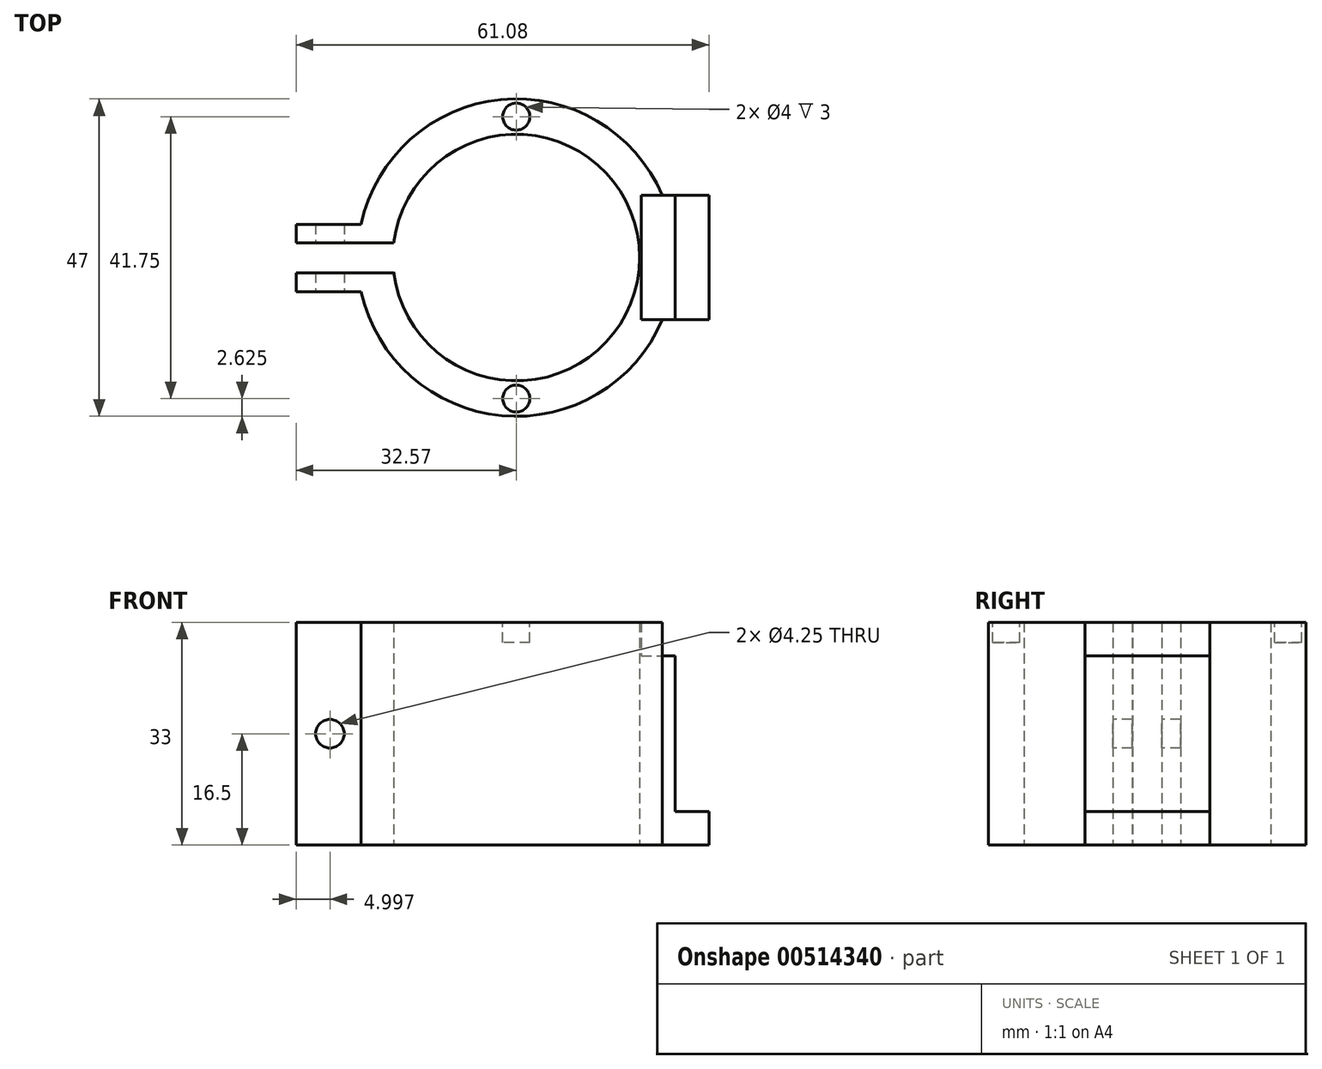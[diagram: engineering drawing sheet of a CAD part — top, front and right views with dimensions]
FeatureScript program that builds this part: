
annotation { "Feature Type Name" : "Feature", "Feature Type Description" : "" }
export const myFeature = defineFeature(function(context is Context, id is Id, definition is map)
    precondition{}
    {
        {
            var Q0;
            Q0=qCreatedBy(makeId("Top.planeOp"),FACE);
            var sketch = newSketch(context, id + "F0", { "sketchPlane" : qUnion([Q0])});
            skCircle(sketch, "E0", {"center": v(0, 0) * mm, "radius": 23.5 * mm});
            skCircle(sketch, "E1", {"center": v(0, 0) * mm, "radius": 18.25 * mm});
            skLineSegment(sketch, "E2.bottom", {"start": v(-17.57, 4.92) * mm, "end": v(-32.57, 4.92) * mm});
            skLineSegment(sketch, "E2.top", {"start": v(-17.57, -5.08) * mm, "end": v(-32.57, -5.08) * mm});
            skLineSegment(sketch, "E2.left", {"start": v(-17.57, 4.92) * mm, "end": v(-17.57, -5.08) * mm});
            skLineSegment(sketch, "E2.right", {"start": v(-32.57, 4.92) * mm, "end": v(-32.57, -5.08) * mm});
            skLineSegment(sketch, "E3.bottom", {"start": v(-18.12, 2.15) * mm, "end": v(-32.57, 2.15) * mm});
            skLineSegment(sketch, "E3.top", {"start": v(-18.12, -2.24) * mm, "end": v(-32.57, -2.24) * mm});
            skLineSegment(sketch, "E3.left", {"start": v(-18.12, 2.15) * mm, "end": v(-18.12, -2.24) * mm});
            skLineSegment(sketch, "E3.right", {"start": v(-32.57, 2.15) * mm, "end": v(-32.57, -2.24) * mm});
            skSolve(sketch);
        }
        {
            var Q0;
            {var subQ0=sQuery(id+"F0.wireOp",EDGE,"E2.bottom");var subQ1=sQuery(id+"F0.wireOp",EDGE,"E0");var subQ2=makeQuery(id+"F0.imprint","INTERSECT",VERTEX,{"derivedFrom":[subQ1,subQ0]});Q0=makeQuery(id+"F0.imprint","IMPRINT",FACE,{"disambiguationData":[TD([[makeQuery(id+"F0.imprint","IMPRINT",EDGE,{"disambiguationData":[TD([[subQ2,-1.0]])],"derivedFrom":subQ1}),-1.0]])]});}
            var Q1;
            {var subQ0=sQuery(id+"F0.wireOp",EDGE,"E2.top");var subQ1=sQuery(id+"F0.wireOp",EDGE,"E0");var subQ2=makeQuery(id+"F0.imprint","INTERSECT",VERTEX,{"derivedFrom":[subQ1,subQ0]});Q1=makeQuery(id+"F0.imprint","IMPRINT",FACE,{"disambiguationData":[TD([[makeQuery(id+"F0.imprint","IMPRINT",EDGE,{"disambiguationData":[TD([[subQ2,1.0]])],"derivedFrom":subQ1}),-1.0]])]});}
            var Q2;
            {var subQ3=sQuery(id+"F0.wireOp",EDGE,"E0");var subQ5=sQuery(id+"F0.wireOp",EDGE,"E2.bottom");var subQ9=makeQuery(id+"F0.imprint","INTERSECT",VERTEX,{"derivedFrom":[subQ3,subQ5]});Q2=makeQuery(id+"F0.imprint","IMPRINT",FACE,{"disambiguationData":[TD([[makeQuery(id+"F0.imprint","IMPRINT",EDGE,{"disambiguationData":[TD([[subQ9,1.0]])],"derivedFrom":subQ3}),1.0]])]});}
            var Q3;
            {var subQ0=sQuery(id+"F0.wireOp",EDGE,"E2.bottom");var subQ1=sQuery(id+"F0.wireOp",EDGE,"E0");var subQ2=makeQuery(id+"F0.imprint","INTERSECT",VERTEX,{"derivedFrom":[subQ1,subQ0]});Q3=makeQuery(id+"F0.imprint","IMPRINT",FACE,{"disambiguationData":[TD([[makeQuery(id+"F0.imprint","IMPRINT",EDGE,{"disambiguationData":[TD([[subQ2,-1.0]])],"derivedFrom":subQ1}),1.0]])]});}
            var Q4;
            {var subQ1=sQuery(id+"F0.wireOp",EDGE,"E2.top");var subQ5=sQuery(id+"F0.wireOp",EDGE,"E0");var subQ6=makeQuery(id+"F0.imprint","INTERSECT",VERTEX,{"derivedFrom":[subQ5,subQ1]});Q4=makeQuery(id+"F0.imprint","IMPRINT",FACE,{"disambiguationData":[TD([[makeQuery(id+"F0.imprint","IMPRINT",EDGE,{"disambiguationData":[TD([[subQ6,1.0]])],"derivedFrom":subQ5}),1.0]])]});}
            var Q5;
            Q5=qSketchRegion(id+"F2",true);
            extrude(context, id + "F1", {"entities" : qUnion([Q0, Q1, Q2, Q3, Q4, Q5]), "depth" : 33 * mm});
        }
        {
            var Q0;
            Q0=makeQuery(id+"F1.opExtrude","SWEPT_FACE",FACE,{"disambiguationData":[OSD([sQuery(id+"F0.wireOp",EDGE,"E2.top")])]});
            var sketch = newSketch(context, id + "F2", { "sketchPlane" : qUnion([Q0])});
            skCircle(sketch, "E4", {"center": v(-27.57, 16.5) * mm, "radius": 2.12 * mm});
            skSolve(sketch);
        }
        {
            var Q0;
            Q0=qCreatedBy(makeId("Top.planeOp"),FACE);
            var sketch = newSketch(context, id + "F3", { "sketchPlane" : qUnion([Q0])});
            skLineSegment(sketch, "E5.bottom", {"start": v(23.5, 9.25) * mm, "end": v(21.63, 9.25) * mm});
            skLineSegment(sketch, "E5.top", {"start": v(23.5, -9.22) * mm, "end": v(21.63, -9.22) * mm});
            skLineSegment(sketch, "E5.left", {"start": v(23.5, 9.25) * mm, "end": v(23.5, -9.22) * mm});
            skLineSegment(sketch, "E5.right", {"start": v(21.63, 9.25) * mm, "end": v(21.63, -9.22) * mm});
            skSolve(sketch);
        }
        {
            var Q0;
            Q0=makeQuery(id+"F3.imprint","IMPRINT",FACE,{"disambiguationData":[TD([[makeQuery(id+"F3.imprint","IMPRINT",EDGE,{"derivedFrom":sQuery(id+"F3.wireOp",EDGE,"E5.bottom")}),1.0]])]});
            extrude(context, id + "F4", {"entities" : qUnion([Q0]), "operationType" : NewBodyOperationType.ADD, "depth" : 33 * mm});
        }
        {
            var Q0;
            Q0=makeQuery(id+"F4.boolean.opBoolean","MERGE",FACE,{"derivedFrom":[makeQuery(id+"F1.opExtrude","CAP_FACE",FACE,{"disambiguationData":[OSD([sQuery(id+"F0.wireOp",EDGE,"E0"),sQuery(id+"F0.wireOp",EDGE,"E1"),sQuery(id+"F0.wireOp",EDGE,"E2.bottom"),sQuery(id+"F0.wireOp",EDGE,"E2.top"),sQuery(id+"F0.wireOp",EDGE,"E2.right"),sQuery(id+"F0.wireOp",EDGE,"E3.bottom"),sQuery(id+"F0.wireOp",EDGE,"E3.top"),sQuery(id+"F0.wireOp",EDGE,"E3.left")])],"isStart":false}),makeQuery(id+"FjpIeYwHbn2ZtRx_1.opExtrude","CAP_FACE",FACE,{"disambiguationData":[OSD([sQuery(id+"FtckRxJgdQJHr4S_1.wireOp",EDGE,"LJ84nlMf-35ZW-CVmp-M2o7-AWeaV5Od0gmK.bottom"),sQuery(id+"FtckRxJgdQJHr4S_1.wireOp",EDGE,"LJ84nlMf-35ZW-CVmp-M2o7-AWeaV5Od0gmK.top"),sQuery(id+"FtckRxJgdQJHr4S_1.wireOp",EDGE,"LJ84nlMf-35ZW-CVmp-M2o7-AWeaV5Od0gmK.left"),sQuery(id+"FtckRxJgdQJHr4S_1.wireOp",EDGE,"LJ84nlMf-35ZW-CVmp-M2o7-AWeaV5Od0gmK.right")])],"isStart":false}),makeQuery(id+"F4.opExtrude","CAP_FACE",FACE,{"disambiguationData":[OSD([sQuery(id+"F3.wireOp",EDGE,"E5.bottom"),sQuery(id+"F3.wireOp",EDGE,"E5.top"),sQuery(id+"F3.wireOp",EDGE,"E5.left"),sQuery(id+"F3.wireOp",EDGE,"E5.right")])],"isStart":false})]});
            var sketch = newSketch(context, id + "F5", { "sketchPlane" : qUnion([Q0])});
            skCircle(sketch, "E6", {"center": v(0, 20.88) * mm, "radius": 2 * mm});
            skCircle(sketch, "E7.1.0.0", {"center": v(0, -20.88) * mm, "radius": 2 * mm});
            skLineSegment(sketch, "E7.direction1", {"start": v(0, 20.88) * mm, "end": v(0, -20.88) * mm, "construction": true});
            skSolve(sketch);
        }
        {
            var Q0;
            Q0=qSketchRegion(id+"F5",true);
            var Q1;
            Q1=sQuery(id+"F5.wireOp",EDGE,"E6");
            var Q2;
            Q2=sQuery(id+"F5.wireOp",EDGE,"E7.1.0.0");
            extrude(context, id + "F6", {"entities" : qUnion([Q0]), "operationType" : NewBodyOperationType.REMOVE, "surfaceEntities" : qUnion([Q1, Q2]), "oppositeDirection" : true, "depth" : 3 * mm});
        }
        {
            var Q0;
            Q0=makeQuery(id+"F4.opExtrude","SWEPT_FACE",FACE,{"disambiguationData":[OSD([sQuery(id+"F3.wireOp",EDGE,"E5.left")])]});
            var sketch = newSketch(context, id + "F7", { "sketchPlane" : qUnion([Q0])});
            skLineSegment(sketch, "E8.bottom", {"start": v(-9.22, 5) * mm, "end": v(9.28, 5) * mm});
            skLineSegment(sketch, "E8.top", {"start": v(-9.22, 0) * mm, "end": v(9.28, 0) * mm});
            skLineSegment(sketch, "E8.left", {"start": v(-9.22, 5) * mm, "end": v(-9.22, 0) * mm});
            skLineSegment(sketch, "E8.right", {"start": v(9.28, 5) * mm, "end": v(9.28, 0) * mm});
            skLineSegment(sketch, "E9.bottom", {"start": v(-9.25, 33) * mm, "end": v(9.25, 33) * mm});
            skLineSegment(sketch, "E9.top", {"start": v(-9.25, 28) * mm, "end": v(9.25, 28) * mm});
            skLineSegment(sketch, "E9.left", {"start": v(-9.25, 33) * mm, "end": v(-9.25, 28) * mm});
            skLineSegment(sketch, "E9.right", {"start": v(9.25, 33) * mm, "end": v(9.25, 28) * mm});
            skSolve(sketch);
        }
        {
            var Q0;
            {var subQ0=sQuery(id+"F7.wireOp",EDGE,"E9.right");Q0=makeQuery(id+"F7.imprint","IMPRINT",FACE,{"disambiguationData":[TD([[makeQuery(id+"F7.imprint","IMPRINT",EDGE,{"derivedFrom":subQ0}),-1.0]])]});}
            extrude(context, id + "F8", {"entities" : qUnion([Q0]), "operationType" : NewBodyOperationType.REMOVE, "oppositeDirection" : true, "depth" : 5 * mm});
        }
        {
            var Q0;
            {var subQ0=sQuery(id+"F7.wireOp",EDGE,"E8.left");Q0=makeQuery(id+"F7.imprint","IMPRINT",FACE,{"disambiguationData":[TD([[makeQuery(id+"F7.imprint","IMPRINT",EDGE,{"derivedFrom":subQ0}),1.0]])]});}
            extrude(context, id + "F9", {"entities" : qUnion([Q0]), "operationType" : NewBodyOperationType.ADD, "depth" : 5 * mm});
        }
        {
            var Q0;
            Q0=makeQuery(id+"F2.imprint","IMPRINT",FACE,{"disambiguationData":[TD([[makeQuery(id+"F2.imprint","IMPRINT",EDGE,{"derivedFrom":sQuery(id+"F2.wireOp",EDGE,"E4")}),1.0]])]});
            extrude(context, id + "F10", {"entities" : qUnion([Q0]), "operationType" : NewBodyOperationType.REMOVE, "oppositeDirection" : true, "depth" : 25 * mm});
        }
    });
